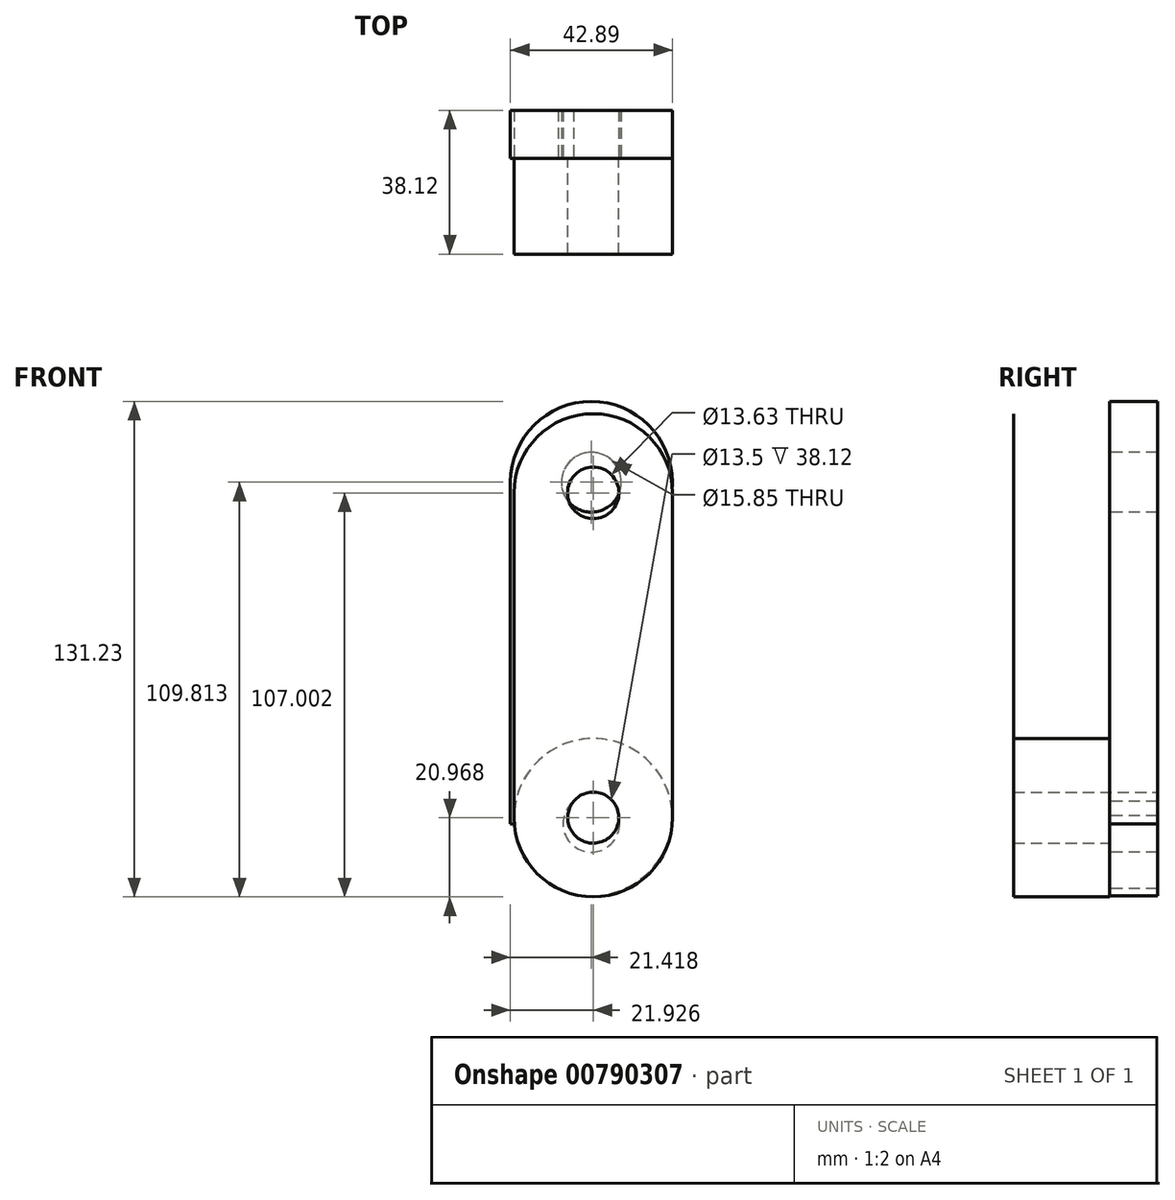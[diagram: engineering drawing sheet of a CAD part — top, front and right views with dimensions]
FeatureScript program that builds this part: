
annotation { "Feature Type Name" : "Feature", "Feature Type Description" : "" }
export const myFeature = defineFeature(function(context is Context, id is Id, definition is map)
    precondition{}
    {
        {
            var Q0;
            Q0=qCreatedBy(makeId("Front.planeOp"),FACE);
            var sketch = newSketch(context, id + "F0", { "sketchPlane" : qUnion([Q0])});
            skLineSegment(sketch, "E0.left", {"start": v(-48.56, 39.4) * mm, "end": v(-48.56, -46.63) * mm});
            skLineSegment(sketch, "E0.right", {"start": v(-6.63, 39.4) * mm, "end": v(-6.63, -46.63) * mm});
            skArc(sketch, "E1", {"start": v(-6.63, 39.4) * mm, "mid": v(-27.6, 60.37) * mm, "end": v(-48.56, 39.4) * mm});
            skArc(sketch, "E2", {"start": v(-48.56, -46.63) * mm, "mid": v(-27.6, -67.6) * mm, "end": v(-6.63, -46.63) * mm});
            skCircle(sketch, "E3", {"center": v(-27.6, 39.4) * mm, "radius": 6.82 * mm});
            skCircle(sketch, "E4", {"center": v(-27.6, -46.63) * mm, "radius": 6.75 * mm});
            skSolve(sketch);
        }
        {
            var Q0;
            Q0=makeQuery(id+"F0.imprint","IMPRINT",FACE,{"disambiguationData":[TD([[makeQuery(id+"F0.imprint","IMPRINT",EDGE,{"derivedFrom":sQuery(id+"F0.wireOp",EDGE,"E0.left")}),1.0]])]});
            extrude(context, id + "F1", {"entities" : qUnion([Q0]), "depth" : 1 / 50.8 * mm, "offsetDistance" : 25.4 * mm});
        }
        {
            var Q0;
            Q0=makeQuery(id+"F1.opExtrude","CAP_FACE",FACE,{"disambiguationData":[OSD([sQuery(id+"F0.wireOp",EDGE,"E0.left"),sQuery(id+"F0.wireOp",EDGE,"E0.right"),sQuery(id+"F0.wireOp",EDGE,"E1"),sQuery(id+"F0.wireOp",EDGE,"E2"),sQuery(id+"F0.wireOp",EDGE,"E3"),sQuery(id+"F0.wireOp",EDGE,"E4")])],"isStart":true});
            var sketch = newSketch(context, id + "F2", { "sketchPlane" : qUnion([Q0])});
            skCircle(sketch, "E5", {"center": v(27.6, -46.63) * mm, "radius": 20.97 * mm});
            skSolve(sketch);
        }
        {
            var Q0;
            {var subQ0=sQuery(id+"F2.wireOp",EDGE,"E5");Q0=makeQuery(id+"F2.imprint","IMPRINT",FACE,{"disambiguationData":[TD([[makeQuery(id+"F2.imprint","IMPRINT",EDGE,{"disambiguationData":[OD(0.0)],"derivedFrom":subQ0}),1.0]])]});}
            extrude(context, id + "F3", {"entities" : qUnion([Q0]), "operationType" : NewBodyOperationType.ADD, "depth" : 25.4 * mm, "offsetDistance" : 25.4 * mm});
        }
        {
            var Q0;
            Q0=makeQuery(id+"F3.opExtrude","CAP_FACE",FACE,{"disambiguationData":[OSD([sQuery(id+"F0.wireOp",EDGE,"E4"),sQuery(id+"F2.wireOp",EDGE,"E5")])],"isStart":false});
            var sketch = newSketch(context, id + "F4", { "sketchPlane" : qUnion([Q0])});
            skLineSegment(sketch, "E6.bottom", {"start": v(6.69, -48.22) * mm, "end": v(49.52, -48.22) * mm});
            skLineSegment(sketch, "E6.top", {"start": v(6.69, 42.21) * mm, "end": v(49.52, 42.21) * mm});
            skLineSegment(sketch, "E6.left", {"start": v(6.69, -48.22) * mm, "end": v(6.69, 42.21) * mm});
            skLineSegment(sketch, "E6.right", {"start": v(49.52, -48.22) * mm, "end": v(49.52, 42.21) * mm});
            skArc(sketch, "E7", {"start": v(6.69, -48.22) * mm, "mid": v(28.1, -67.3) * mm, "end": v(49.52, -48.22) * mm});
            skCircle(sketch, "E8", {"center": v(28.1, -48.22) * mm, "radius": 7.53 * mm});
            skArc(sketch, "E9", {"start": v(49.52, 42.21) * mm, "mid": v(28.1, 63.63) * mm, "end": v(6.69, 42.21) * mm});
            skCircle(sketch, "E10", {"center": v(28.1, 42.21) * mm, "radius": 7.92 * mm});
            skSolve(sketch);
        }
        {
            var Q0;
            {var subQ0=sQuery(id+"F4.wireOp",EDGE,"E8");var subQ1=sQuery(id+"F4.wireOp",EDGE,"E6.bottom");var subQ2=makeQuery(id+"F4.imprint","INTERSECT",VERTEX,{"disambiguationData":[OD(1.0)],"derivedFrom":[subQ1,subQ0]});Q0=makeQuery(id+"F4.imprint","IMPRINT",FACE,{"disambiguationData":[TD([[makeQuery(id+"F4.imprint","IMPRINT",EDGE,{"disambiguationData":[TD([[subQ2,-1.0]])],"derivedFrom":subQ1}),1.0]])]});}
            var Q1;
            {var subQ1=sQuery(id+"F4.wireOp",EDGE,"E6.right");Q1=makeQuery(id+"F4.imprint","IMPRINT",FACE,{"disambiguationData":[TD([[makeQuery(id+"F4.imprint","IMPRINT",EDGE,{"derivedFrom":subQ1}),1.0]])]});}
            var Q2;
            {var subQ0=sQuery(id+"F4.wireOp",EDGE,"E8");var subQ1=sQuery(id+"F4.wireOp",EDGE,"E6.bottom");var subQ3=makeQuery(id+"F4.imprint","INTERSECT",VERTEX,{"disambiguationData":[OD(1.0)],"derivedFrom":[subQ1,subQ0]});Q2=makeQuery(id+"F4.imprint","IMPRINT",FACE,{"disambiguationData":[TD([[makeQuery(id+"F4.imprint","IMPRINT",EDGE,{"disambiguationData":[TD([[subQ3,-1.0]])],"derivedFrom":subQ1}),-1.0]])]});}
            var Q3;
            {var subQ0=sQuery(id+"F4.wireOp",EDGE,"E9");Q3=makeQuery(id+"F4.imprint","IMPRINT",FACE,{"disambiguationData":[TD([[makeQuery(id+"F4.imprint","IMPRINT",EDGE,{"derivedFrom":subQ0}),1.0]])]});}
            extrude(context, id + "F5", {"entities" : qUnion([Q0, Q1, Q2, Q3]), "operationType" : NewBodyOperationType.ADD, "depth" : 12.7 * mm, "offsetDistance" : 25.4 * mm});
        }
    });
